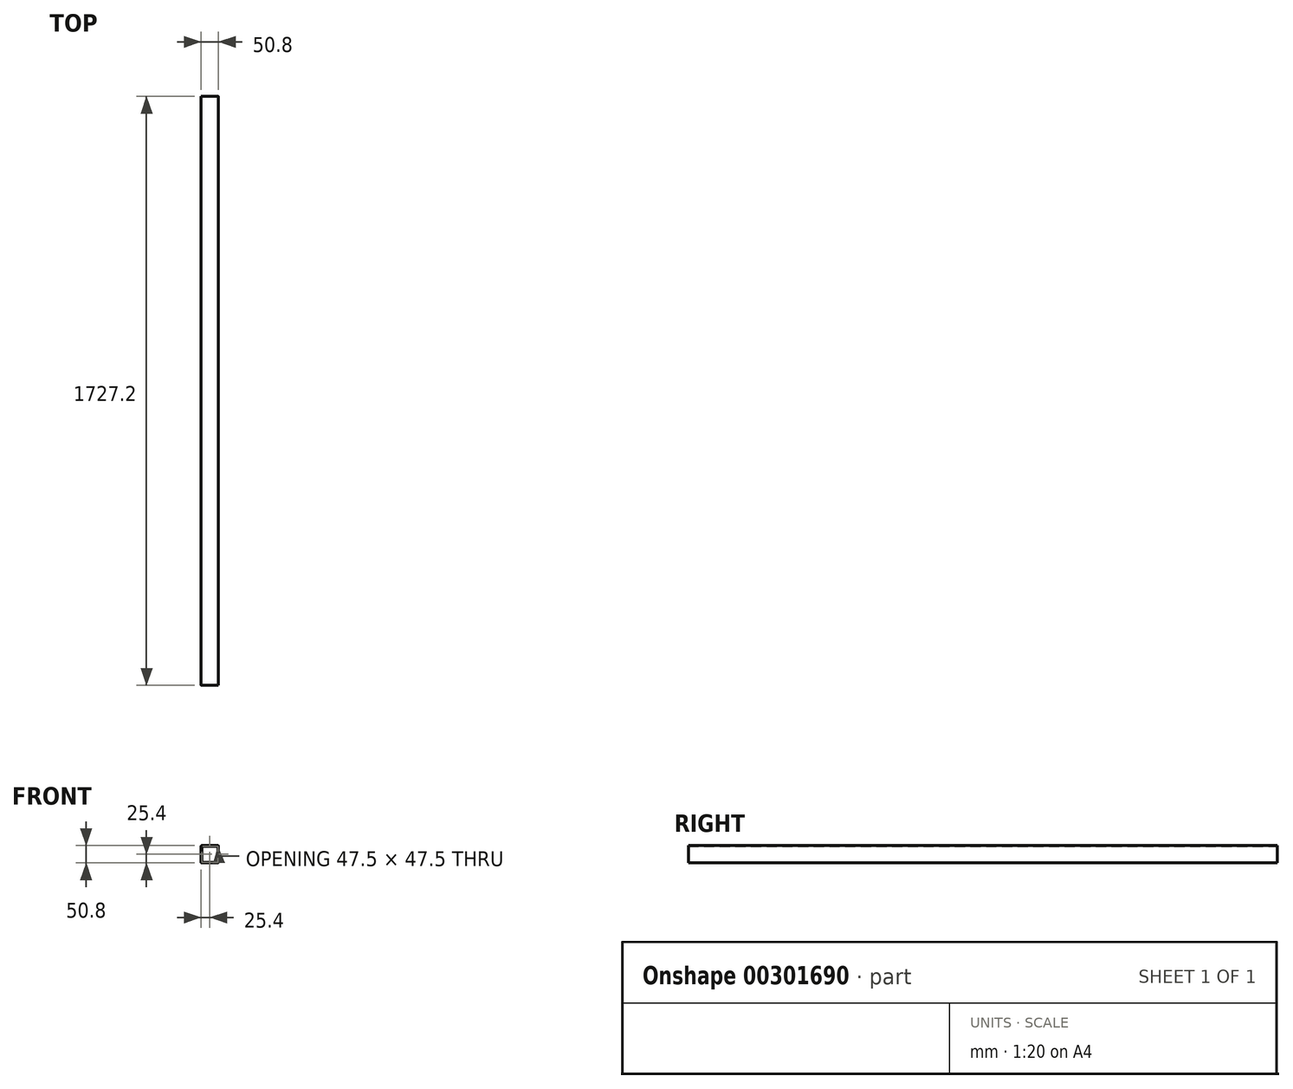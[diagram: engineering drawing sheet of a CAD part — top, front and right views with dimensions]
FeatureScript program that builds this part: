
annotation { "Feature Type Name" : "Feature", "Feature Type Description" : "" }
export const myFeature = defineFeature(function(context is Context, id is Id, definition is map)
    precondition{}
    {
        {
            var Q0;
            Q0=qCreatedBy(makeId("Front.planeOp"),FACE);
            var sketch = newSketch(context, id + "F0", { "sketchPlane" : qUnion([Q0])});
            skLineSegment(sketch, "E0.bottom", {"start": v(-23.75, -25.4) * mm, "end": v(23.75, -25.4) * mm});
            skLineSegment(sketch, "E0.top", {"start": v(-23.75, 25.4) * mm, "end": v(23.75, 25.4) * mm});
            skLineSegment(sketch, "E0.left", {"start": v(-25.4, -23.75) * mm, "end": v(-25.4, 23.75) * mm});
            skLineSegment(sketch, "E0.right", {"start": v(25.4, -23.75) * mm, "end": v(25.4, 23.75) * mm});
            skPoint(sketch, "E0.middle", {"position": v(0, 0) * mm});
            skLineSegment(sketch, "E1.0", {"start": v(-22.1, 23.75) * mm, "end": v(22.1, 23.75) * mm});
            skLineSegment(sketch, "E1.1", {"start": v(-23.75, -22.1) * mm, "end": v(-23.75, 22.1) * mm});
            skLineSegment(sketch, "E1.2", {"start": v(-22.1, -23.75) * mm, "end": v(22.1, -23.75) * mm});
            skLineSegment(sketch, "E1.3", {"start": v(23.75, -22.1) * mm, "end": v(23.75, 22.1) * mm});
            skPoint(sketch, "E2.visualSharp", {"position": v(-23.75, 23.75) * mm});
            skArc(sketch, "E2.filletArc", {"start": v(-22.1, 23.75) * mm, "mid": v(-23.27, 23.27) * mm, "end": v(-23.75, 22.1) * mm});
            skPoint(sketch, "E3.visualSharp", {"position": v(-25.4, 25.4) * mm});
            skArc(sketch, "E3.filletArc", {"start": v(-23.75, 25.4) * mm, "mid": v(-24.92, 24.92) * mm, "end": v(-25.4, 23.75) * mm});
            skPoint(sketch, "E4.visualSharp", {"position": v(23.75, 23.75) * mm});
            skArc(sketch, "E4.filletArc", {"start": v(23.75, 22.1) * mm, "mid": v(23.27, 23.27) * mm, "end": v(22.1, 23.75) * mm});
            skPoint(sketch, "E5.visualSharp", {"position": v(23.75, -23.75) * mm});
            skArc(sketch, "E5.filletArc", {"start": v(22.1, -23.75) * mm, "mid": v(23.27, -23.27) * mm, "end": v(23.75, -22.1) * mm});
            skPoint(sketch, "E6.visualSharp", {"position": v(-23.75, -23.75) * mm});
            skArc(sketch, "E6.filletArc", {"start": v(-23.75, -22.1) * mm, "mid": v(-23.27, -23.27) * mm, "end": v(-22.1, -23.75) * mm});
            skPoint(sketch, "E7.visualSharp", {"position": v(-25.4, -25.4) * mm});
            skArc(sketch, "E7.filletArc", {"start": v(-25.4, -23.75) * mm, "mid": v(-24.92, -24.92) * mm, "end": v(-23.75, -25.4) * mm});
            skPoint(sketch, "E8.visualSharp", {"position": v(25.4, -25.4) * mm});
            skArc(sketch, "E8.filletArc", {"start": v(23.75, -25.4) * mm, "mid": v(24.92, -24.92) * mm, "end": v(25.4, -23.75) * mm});
            skPoint(sketch, "E9.visualSharp", {"position": v(25.4, 25.4) * mm});
            skArc(sketch, "E9.filletArc", {"start": v(25.4, 23.75) * mm, "mid": v(24.92, 24.92) * mm, "end": v(23.75, 25.4) * mm});
            skSolve(sketch);
        }
        {
            var Q0;
            Q0 = qSketchRegion(id + "F0", true);
            extrude(context, id + "F1", {"entities" : qUnion([Q0]), "depth" : 1727.2 * mm});
        }
    });
